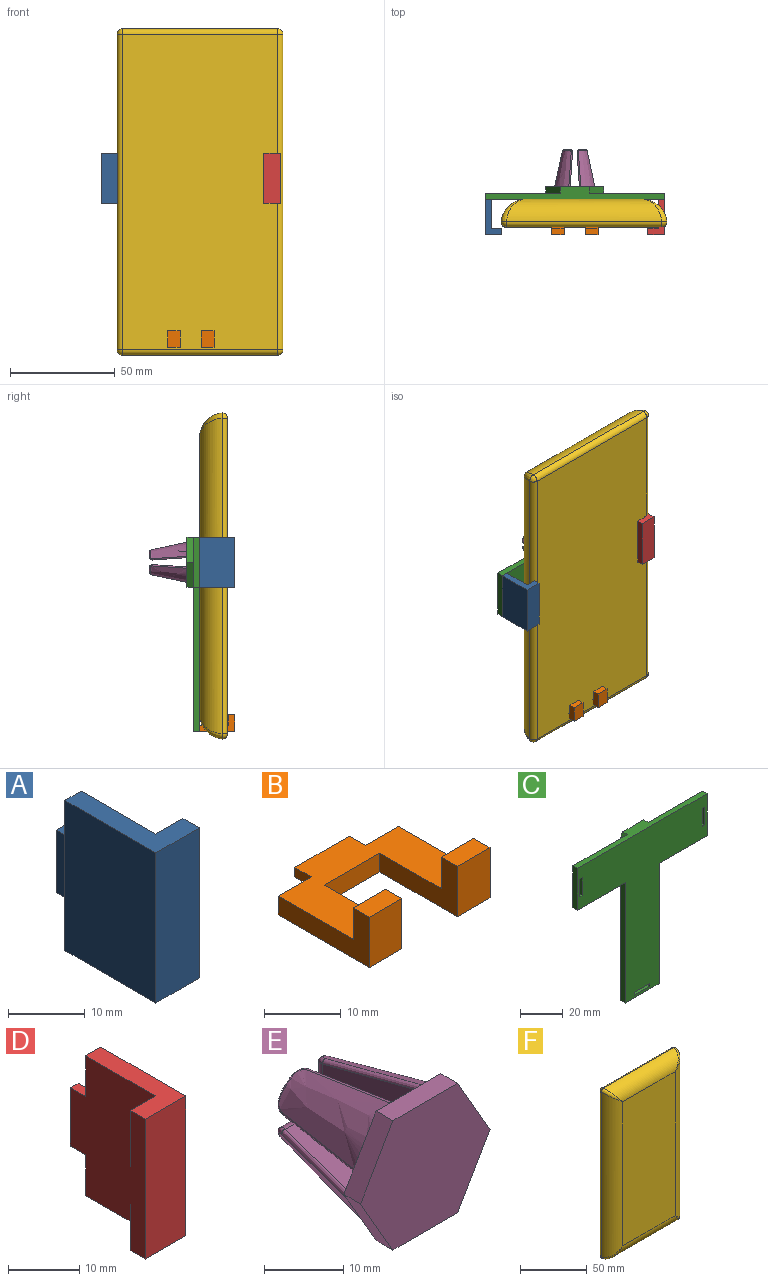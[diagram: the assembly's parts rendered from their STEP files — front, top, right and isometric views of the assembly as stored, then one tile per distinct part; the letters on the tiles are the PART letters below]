
ASSEMBLY  parts=6 mates=5
PART A: 12 faces, bbox 8x19.8x24 mm
  f0: plane 16.8x8mm, normal (0,0,-1), area 65.4mm2, adj f1,f4,f5,f6,f7,f11
  f1: plane 24x16.8mm, normal (1,0,0), area 361.2mm2, adj f0,f2,f3,f7,f8,f10,f11
  f2: plane 16.8x8mm, normal (0,0,1), area 65.4mm2, adj f1,f4,f5,f6,f7,f11
  f3: plane 10x1.5mm, normal (0,1,0), area 15mm2, adj f1,f8,f9,f10
  f4: plane 24x16.8mm, normal (-1,0,0), area 403.2mm2, adj f0,f2,f6,f11
  f5: plane 24x3mm, normal (1,0,0), area 72mm2, adj f0,f2,f6,f7
  f6: plane 24x8mm, normal (0,-1,0), area 192mm2, adj f0,f2,f4,f5
  f7: plane 24x5mm, normal (0,1,0), area 120mm2, adj f0,f1,f2,f5
  f8: plane 3x1.5mm, normal (0,0,1), area 4.5mm2, adj f1,f3,f9,f11
  f9: plane 10x3mm, normal (-1,0,0), area 30mm2, adj f3,f8,f10,f11
  f10: plane 3x1.5mm, normal (0,0,-1), area 4.5mm2, adj f1,f3,f9,f11
  f11: plane 24x3mm, normal (0,1,0), area 57mm2, adj f0,f1,f2,f4,f8,f9,f10
PART B: 18 faces, bbox 22.2x19.8x8 mm
  f0: plane 10x1.5mm, normal (0,1,0), area 15mm2, adj f1,f2,f3,f4
  f1: plane 22.2x16.8mm, normal (0,0,1), area 221.1mm2, adj f0,f3,f4,f5,f6,f7,f9,f12
  f2: plane 10x3mm, normal (0,0,-1), area 30mm2, adj f0,f3,f4,f5
  f3: plane 3x1.5mm, normal (-1,0,0), area 4.5mm2, adj f0,f1,f2,f5
  f4: plane 3x1.5mm, normal (1,0,0), area 4.5mm2, adj f0,f1,f2,f5
  f5: plane 22.2x3mm, normal (0,1,0), area 51.6mm2, adj f1,f2,f3,f4,f7,f8,f16
  f6: plane 14.3x8mm, normal (1,0,0), area 57.9mm2, adj f1,f8,f9,f10,f11,f17
  f7: plane 16.8x8mm, normal (-1,0,0), area 65.4mm2, adj f1,f5,f8,f9,f10,f11
  f8: plane 22.2x16.8mm, normal (0,0,-1), area 227.1mm2, adj f5,f6,f7,f11,f12,f15,f16,f17
  f9: plane 6x5mm, normal (0,1,0), area 30mm2, adj f1,f6,f7,f10
  f10: plane 6x3mm, normal (0,0,1), area 18mm2, adj f6,f7,f9,f11
  f11: plane 8x6mm, normal (0,-1,0), area 48mm2, adj f6,f7,f8,f10
  f12: plane 14.3x8mm, normal (-1,0,0), area 57.9mm2, adj f1,f8,f13,f14,f15,f17
  f13: plane 6x5mm, normal (0,1,0), area 30mm2, adj f1,f12,f14,f16
  f14: plane 6x3mm, normal (0,0,1), area 18mm2, adj f12,f13,f15,f16
  f15: plane 8x6mm, normal (0,-1,0), area 48mm2, adj f8,f12,f14,f16
  f16: plane 16.8x8mm, normal (1,0,0), area 65.4mm2, adj f1,f5,f8,f13,f14,f15
  f17: plane 10.2x3mm, normal (0,-1,0), area 30.6mm2, adj f1,f6,f8,f12
PART C: 35 faces, bbox 85.8x6x93 mm
  f0: plane 69x3mm, normal (-1,0,0), area 207mm2, adj f2,f3,f4,f5
  f1: plane 69x3mm, normal (1,0,0), area 207mm2, adj f2,f3,f4,f9
  f2: plane 22.2x3mm, normal (0,0,-1), area 66.6mm2, adj f0,f1,f3,f4
  f3: plane 93x85.8mm, normal (0,1,0), area 3043.7mm2, adj f0,f1,f2,f5,f6,f7,f8,f9
  f4: plane 93x85.8mm, normal (0,-1,0), area 3542.5mm2, adj f0,f1,f2,f5,f6,f7,f8,f9
  f5: plane 31.8x3mm, normal (0,0,-1), area 95.4mm2, adj f0,f3,f4,f8
  f6: plane 24x3mm, normal (1,0,0), area 72mm2, adj f3,f4,f7,f9
  f7: plane 85.8x6mm, normal (0,0,1), area 299mm2, adj f3,f4,f6,f8,f16,f17,f21
  f8: plane 24x3mm, normal (-1,0,0), area 72mm2, adj f3,f4,f5,f7
  f9: plane 31.8x3mm, normal (0,0,-1), area 95.4mm2, adj f1,f3,f4,f6
  f10: plane 10.1x5.83mm, normal (0.87,0,-0.5), area 35mm2, adj f11,f20,f21,f22
  f11: plane 10.1x5.83mm, normal (0.87,0,0.5), area 35mm2, adj f10,f12,f21,f22
  f12: plane 11.66x3mm, normal (0,0,1), area 35mm2, adj f11,f13,f21,f22
  f13: plane 10.1x5.83mm, normal (-0.87,0,0.5), area 35mm2, adj f12,f14,f21,f22
  f14: plane 10.1x5.83mm, normal (-0.87,0,-0.5), area 35mm2, adj f13,f20,f21,f22
  f15: plane 12x6.93mm, normal (-0.87,0,-0.5), area 41.6mm2, adj f3,f16,f19,f21
  f16: plane 12x6.93mm, normal (-0.87,0,0.5), area 41.6mm2, adj f3,f7,f15,f21
  f17: plane 12x6.93mm, normal (0.87,0,0.5), area 41.6mm2, adj f3,f7,f18,f21
  f18: plane 12x6.93mm, normal (0.87,0,-0.5), area 41.6mm2, adj f3,f17,f19,f21
  f19: plane 13.86x3mm, normal (0,0,-1), area 41.6mm2, adj f3,f15,f18,f21
  f20: plane 11.66x3mm, normal (0,0,-1), area 35mm2, adj f10,f14,f21,f22
  f21: plane 27.71x24mm, normal (0,1,0), area 145.5mm2, adj f7,f10,f11,f12,f13,f14,f15,f16
  f22: plane 23.33x20.2mm, normal (0,1,0), area 353.4mm2, adj f10,f11,f12,f13,f14,f20
  f23: plane 10.1x3mm, normal (1,0,0), area 30.3mm2, adj f3,f4,f24,f25
  f24: plane 3x1.6mm, normal (0,0,-1), area 4.8mm2, adj f3,f4,f23,f26
  f25: plane 3x1.6mm, normal (0,0,1), area 4.8mm2, adj f3,f4,f23,f26
  f26: plane 10.1x3mm, normal (-1,0,0), area 30.3mm2, adj f3,f4,f24,f25
  f27: plane 10.1x3mm, normal (0,0,1), area 30.3mm2, adj f3,f4,f28,f29
  f28: plane 3x1.6mm, normal (1,0,0), area 4.8mm2, adj f3,f4,f27,f30
  f29: plane 3x1.6mm, normal (-1,0,0), area 4.8mm2, adj f3,f4,f27,f30
  f30: plane 10.1x3mm, normal (0,0,-1), area 30.3mm2, adj f3,f4,f28,f29
  f31: plane 10.1x3mm, normal (1,0,0), area 30.3mm2, adj f3,f4,f32,f33
  f32: plane 3x1.6mm, normal (0,0,-1), area 4.8mm2, adj f3,f4,f31,f34
  f33: plane 3x1.6mm, normal (0,0,1), area 4.8mm2, adj f3,f4,f31,f34
  f34: plane 10.1x3mm, normal (-1,0,0), area 30.3mm2, adj f3,f4,f32,f33
PART D: 12 faces, bbox 8x19.8x24 mm
  f0: plane 16.8x8mm, normal (0,0,-1), area 65.4mm2, adj f1,f3,f5,f6,f7,f11
  f1: plane 24x16.8mm, normal (1,0,0), area 403.2mm2, adj f0,f4,f6,f11
  f2: plane 10x1.5mm, normal (0,1,0), area 15mm2, adj f3,f8,f9,f10
  f3: plane 24x16.8mm, normal (-1,0,0), area 361.2mm2, adj f0,f2,f4,f7,f8,f10,f11
  f4: plane 16.8x8mm, normal (0,0,1), area 65.4mm2, adj f1,f3,f5,f6,f7,f11
  f5: plane 24x3mm, normal (-1,0,0), area 72mm2, adj f0,f4,f6,f7
  f6: plane 24x8mm, normal (0,-1,0), area 192mm2, adj f0,f1,f4,f5
  f7: plane 24x5mm, normal (0,1,0), area 120mm2, adj f0,f3,f4,f5
  f8: plane 3x1.5mm, normal (0,0,-1), area 4.5mm2, adj f2,f3,f9,f11
  f9: plane 10x3mm, normal (1,0,0), area 30mm2, adj f2,f8,f10,f11
  f10: plane 3x1.5mm, normal (0,0,1), area 4.5mm2, adj f2,f3,f9,f11
  f11: plane 24x3mm, normal (0,1,0), area 57mm2, adj f0,f1,f3,f4,f8,f9,f10
PART E: 60 faces, bbox 23.2x23.4x20.6 mm
  f0: bspline ~17.61x8.12mm, area 143.4mm2, adj f4,f18,f19,f20,f48,f52
  f1: bspline ~17.61x8.12mm, area 143.4mm2, adj f4,f22,f23,f24,f43,f47
  f2: bspline ~17.61x8.12mm, area 143.4mm2, adj f4,f26,f27,f28,f38,f42
  f3: bspline ~17.61x8.12mm, area 143.4mm2, adj f4,f30,f31,f32,f33,f37
  f4: plane 23.15x20.06mm, normal (0,1,0), area 188.5mm2, adj f0,f1,f2,f3,f6,f7,f9,f10
  f5: plane 2.36x2.36mm, normal (0,1,0), area 3.3mm2, adj f31,f34,f36
  f6: plane 16.4x7.48mm, normal (-1,-0.07,0), area 85.4mm2, adj f4,f29,f32,f34
  f7: plane 16.4x7.48mm, normal (0,-0.07,-1), area 85.4mm2, adj f4,f29,f30,f36
  f8: plane 2.36x2.36mm, normal (0,1,0), area 3.3mm2, adj f27,f39,f41
  f9: plane 16.4x7.48mm, normal (1,-0.07,0), area 85.4mm2, adj f4,f25,f28,f39
  f10: plane 16.4x7.48mm, normal (0,-0.07,-1), area 85.4mm2, adj f4,f25,f26,f41
  f11: plane 2.36x2.36mm, normal (0,1,0), area 3.3mm2, adj f23,f44,f46
  f12: plane 16.4x7.48mm, normal (-1,-0.07,0), area 85.4mm2, adj f4,f21,f24,f44
  f13: plane 16.4x7.48mm, normal (0,-0.07,1), area 85.4mm2, adj f4,f21,f22,f46
  f14: plane 2.36x2.36mm, normal (0,1,0), area 3.3mm2, adj f19,f49,f51
  f15: plane 16.4x7.48mm, normal (0,-0.07,1), area 85.4mm2, adj f4,f17,f20,f49
  f16: plane 16.4x7.48mm, normal (1,-0.07,0), area 85.4mm2, adj f4,f17,f18,f51
  f17: cylinder r=0.5mm len=16.41mm, axis (-0.07,-1,-0.07), area 12.9mm2, adj f4,f15,f16,f50
  f18: bspline ~22.72x5.45mm, area 15.7mm2, adj f0,f4,f16,f52
  f19: bspline ~3.89x3.54mm, area 2.4mm2, adj f0,f14,f48,f52
  f20: bspline ~22.72x5.45mm, area 15.7mm2, adj f0,f4,f15,f48
  f21: cylinder r=0.5mm len=16.41mm, axis (0.07,-1,-0.07), area 12.9mm2, adj f4,f12,f13,f45
  f22: bspline ~22.72x5.45mm, area 15.7mm2, adj f1,f4,f13,f47
  f23: bspline ~3.89x3.54mm, area 2.4mm2, adj f1,f11,f43,f47
  f24: bspline ~22.72x5.45mm, area 15.7mm2, adj f1,f4,f12,f43
  f25: cylinder r=0.5mm len=16.41mm, axis (-0.07,-1,0.07), area 12.9mm2, adj f4,f9,f10,f40
  f26: bspline ~22.72x5.45mm, area 15.7mm2, adj f2,f4,f10,f42
  f27: bspline ~3.89x3.54mm, area 2.4mm2, adj f2,f8,f38,f42
  f28: bspline ~22.72x5.45mm, area 15.7mm2, adj f2,f4,f9,f38
  f29: cylinder r=0.5mm len=16.41mm, axis (-0.07,1,-0.07), area 12.9mm2, adj f4,f6,f7,f35
  f30: bspline ~20.18x4.91mm, area 15.7mm2, adj f3,f4,f7,f37
  f31: bspline ~3.62x3.43mm, area 2.4mm2, adj f3,f5,f33,f37
  f32: bspline ~20.18x4.91mm, area 15.7mm2, adj f3,f4,f6,f33
  f33: bspline ~2.03x1.75mm, area 1.9mm2, adj f3,f31,f32,f34
  f34: cylinder r=1.5mm len=4mm, axis (0,0,-1), area 7.8mm2, adj f5,f6,f33,f35
  f35: bspline ~1.76x1.5mm, area 0.9mm2, adj f29,f34,f36
  f36: cylinder r=1.5mm len=4mm, axis (-1,0,0), area 7.8mm2, adj f5,f7,f35,f37
  f37: bspline ~1.99x1.93mm, area 1.9mm2, adj f3,f30,f31,f36
  f38: bspline ~1.99x1.93mm, area 1.9mm2, adj f2,f27,f28,f39
  f39: cylinder r=1.5mm len=4mm, axis (0,0,-1), area 7.8mm2, adj f8,f9,f38,f40
  f40: bspline ~1.76x1.5mm, area 0.9mm2, adj f25,f39,f41
  f41: cylinder r=1.5mm len=4mm, axis (1,0,0), area 7.8mm2, adj f8,f10,f40,f42
  f42: bspline ~2.03x1.75mm, area 1.9mm2, adj f2,f26,f27,f41
  f43: bspline ~1.99x1.93mm, area 1.9mm2, adj f1,f23,f24,f44
  f44: cylinder r=1.5mm len=4mm, axis (0,0,1), area 7.8mm2, adj f11,f12,f43,f45
  f45: bspline ~1.76x1.5mm, area 0.9mm2, adj f21,f44,f46
  f46: cylinder r=1.5mm len=4mm, axis (-1,0,0), area 7.8mm2, adj f11,f13,f45,f47
  f47: bspline ~2.03x1.75mm, area 1.9mm2, adj f1,f22,f23,f46
  f48: bspline ~1.99x1.93mm, area 1.9mm2, adj f0,f19,f20,f49
  f49: cylinder r=1.5mm len=4mm, axis (1,0,0), area 7.8mm2, adj f14,f15,f48,f50
  f50: bspline ~1.76x1.5mm, area 0.9mm2, adj f17,f49,f51
  f51: cylinder r=1.5mm len=4mm, axis (0,0,1), area 7.8mm2, adj f14,f16,f50,f52
  f52: bspline ~2.03x1.75mm, area 1.9mm2, adj f0,f18,f19,f51
  f53: plane 11.55x3mm, normal (0,0,1), area 34.6mm2, adj f4,f54,f58,f59
  f54: plane 10x5.77mm, normal (0.87,0,0.5), area 34.6mm2, adj f4,f53,f55,f59
  f55: plane 10x5.77mm, normal (0.87,0,-0.5), area 34.6mm2, adj f4,f54,f56,f59
  f56: plane 11.55x3mm, normal (0,0,-1), area 34.6mm2, adj f4,f55,f57,f59
  f57: plane 10x5.77mm, normal (-0.87,0,-0.5), area 34.6mm2, adj f4,f56,f58,f59
  f58: plane 10x5.77mm, normal (-0.87,0,0.5), area 34.6mm2, adj f4,f53,f57,f59
  f59: plane 23.09x20mm, normal (0,-1,0), area 346.4mm2, adj f53,f54,f55,f56,f57,f58
PART F: 18 faces, bbox 79.3x13.3x156 mm
  f0: plane 132.12x55.42mm, normal (0,-1,0), area 7322.1mm2, adj f10,f13,f14,f17
  f1: plane 151x74.3mm, normal (0,1,0), area 11219.3mm2, adj f3,f4,f7,f8
  f2: sphere r=2.5mm, area 9.8mm2, adj f3,f4,f11
  f3: cylinder r=2.5mm len=74.3mm, axis (-1,0,0), area 291.8mm2, adj f1,f2,f5,f13
  f4: cylinder r=2.5mm len=151mm, axis (0,0,-1), area 593mm2, adj f1,f2,f6,f10
  f5: sphere r=2.5mm, area 13.4mm2, adj f3,f7,f15
  f6: sphere r=2.5mm, area 9.8mm2, adj f4,f8,f12
  f7: cylinder r=2.5mm len=151mm, axis (0,0,1), area 593mm2, adj f1,f5,f9,f17
  f8: cylinder r=2.5mm len=74.3mm, axis (1,0,0), area 291.8mm2, adj f1,f6,f9,f14
  f9: sphere r=2.5mm, area 6.2mm2, adj f7,f8,f16
  f10: cylinder r=12mm len=151mm, axis (0,0,-1), area 2498.2mm2, adj f0,f4,f11,f12
  f11: bspline ~11.94x11.94mm, area 29.5mm2, adj f2,f10,f13
  f12: bspline ~11.94x11.94mm, area 29.5mm2, adj f6,f10,f14
  f13: cylinder r=12mm len=74.3mm, axis (1,0,0), area 1144.6mm2, adj f0,f3,f11,f15
  f14: cylinder r=12mm len=74.3mm, axis (1,0,0), area 1144.6mm2, adj f0,f8,f12,f16
  f15: bspline ~11.94x11.94mm, area 29.4mm2, adj f5,f13,f17
  f16: bspline ~11.94x11.94mm, area 29.5mm2, adj f9,f14,f17
  f17: cylinder r=12mm len=151mm, axis (0,0,-1), area 2498.2mm2, adj f0,f7,f15,f16
PLACE A t=(-81.2,-40.39,27.55)mm
PLACE B t=(-94.2,-40.39,40.65)mm
PLACE C t=(-94.2,-40.39,27.55)mm
PLACE D t=(-107.2,-40.39,27.55)mm
PLACE E t=(-94.2,-57.39,27.55)mm
PLACE F rot(axis=(1,0,0),180deg) t=(-232.27,-73.69,-8.84)mm
MATE fastened B.f0 <-> C.f3  axis (0,1,0) through (-94.2,-57.39,-50.35)mm
MATE fastened E.f59 <-> C.f22  axis (0,-1,0) through (-94.2,-57.39,27.55)mm
MATE planar C.f4 <-> F.f0  axis (0,-1,0) through (-94.2,-60.39,7.81)mm
MATE fastened D.f2 <-> C.f3  axis (0,1,0) through (-52.8,-57.39,27.55)mm
MATE fastened A.f3 <-> C.f3  axis (0,1,0) through (-135.6,-57.39,27.55)mm
